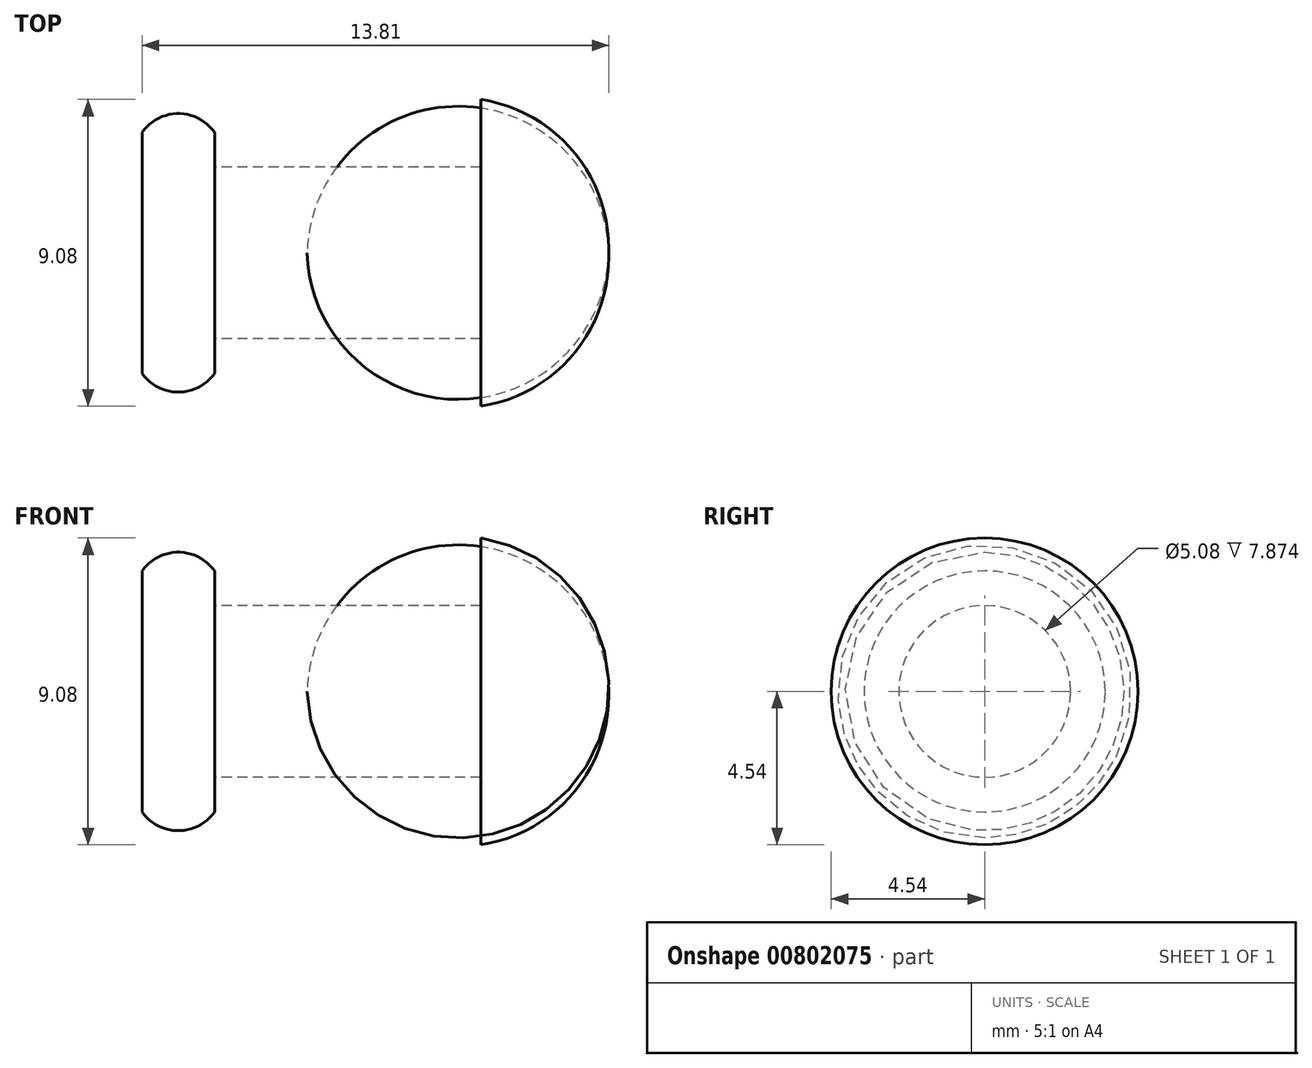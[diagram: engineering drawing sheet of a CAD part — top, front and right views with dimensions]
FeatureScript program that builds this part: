
annotation { "Feature Type Name" : "Feature", "Feature Type Description" : "" }
export const myFeature = defineFeature(function(context is Context, id is Id, definition is map)
    precondition{}
    {
        {
            var Q0;
            Q0=qCreatedBy(makeId("Front.planeOp"),FACE);
            var sketch = newSketch(context, id + "F0", { "sketchPlane" : qUnion([Q0])});
            skLineSegment(sketch, "E0", {"start": v(-0.44, 2.54) * mm, "end": v(7.43, 2.54) * mm});
            skLineSegment(sketch, "E1", {"start": v(7.43, 2.54) * mm, "end": v(7.43, 4.54) * mm});
            skLineSegment(sketch, "E2", {"start": v(-0.44, 2.54) * mm, "end": v(-0.44, 3.57) * mm});
            skArc(sketch, "E3", {"start": v(-0.44, 3.57) * mm, "mid": v(-1.51, 4.12) * mm, "end": v(-2.58, 3.57) * mm});
            skLineSegment(sketch, "E4", {"start": v(0, 0) * mm, "end": v(14.33, 0) * mm, "construction": true});
            skPoint(sketch, "E5", {"position": v(11.22, 0) * mm});
            skArc(sketch, "E6", {"start": v(11.22, 0) * mm, "mid": v(10.19, 2.99) * mm, "end": v(7.43, 4.54) * mm});
            skLineSegment(sketch, "E7", {"start": v(-2.58, 0) * mm, "end": v(11.22, 0) * mm});
            skLineSegment(sketch, "E8", {"start": v(-2.58, 3.57) * mm, "end": v(-2.58, 0) * mm});
            skSolve(sketch);
        }
        {
            var Q0;
            Q0 = qSketchRegion(id + "F0", true);
            var Q1;
            Q1=sQuery(id+"F0.wireOp",EDGE,"E4");
            revolve(context, id + "F1", {"entities" : qUnion([Q0]), "axis" : qUnion([Q1]), "revolveType" : RevolveType.FULL});
        }
    });
